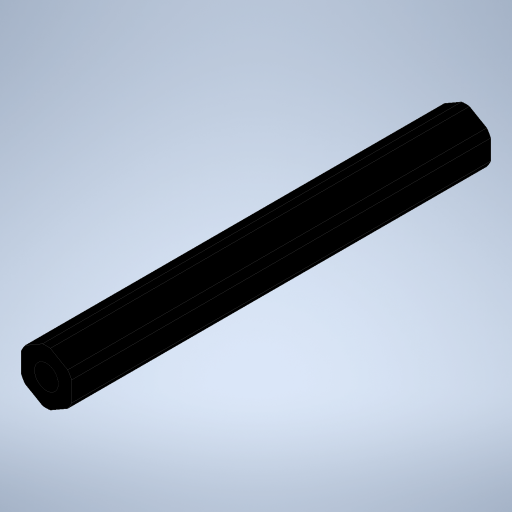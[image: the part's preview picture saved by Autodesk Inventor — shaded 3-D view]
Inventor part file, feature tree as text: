
AUTODESK INVENTOR PART (.ipt)
format: ipt  version: 2023.4 (Build 274418000, 418)  size: 257,536 bytes
history: native  units: in
note: dims shown in document units (in); Inventor stores cm internally (conversion verified against a paired STEP export)
features: extrude x2, projected_geometry x2, hole x1
ambient origin geometry x8: Origin, YZ Plane, XZ Plane, XY Plane, X Axis, Y Axis, Z Axis, Center Point
bodies: Solid1 (feature_tree)
feature tree (5):
  extrude  "Extrusion1"  TaperAngle=0.0deg  [1 undecoded]
  hole  "Hole1"  [1 undecoded]
  extrude  "Extrusion3"  TaperAngle=0.0deg  [1 undecoded]
  projected_geometry  "Project Cut Edges1"
  projected_geometry  "Project Cut Edges2"
note: 3 required parameter values undecoded (feature->parameter linkage not recoverable at this tier; creation-order binding heuristic only, values carry confidence <= 0.55)
